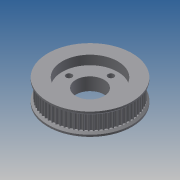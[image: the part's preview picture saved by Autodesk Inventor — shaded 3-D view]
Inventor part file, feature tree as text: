
AUTODESK INVENTOR PART (.ipt)
format: ipt  version: 2013 (Build 170138000, 138)  size: 355,840 bytes
history: native  units: mm
features: extrude x7, sketch x7, pattern_circular x2, chamfer x1, mirror x1
ambient origin geometry x8: Origin, YZ Plane, XZ Plane, XY Plane, X Axis, Y Axis, Z Axis, Center Point
bodies: Solid1 (feature_tree)
feature tree (18):
  extrude  "Extrusion1"  Depth=8.0mm TaperAngle=0.0deg
  extrude  "Extrusion3"  TaperAngle=0.0deg  [1 undecoded]
  extrude  "Extrusion4"  Depth=8.0mm TaperAngle=0.0deg
  pattern_circular  "Circular Pattern1"  Count=70 Angle=360.0deg
  extrude  "Extrusion5"  Depth=2.0mm TaperAngle=0.0deg
  chamfer  "Chamfer1"  Distance=1.0mm Angle=45.0deg
  mirror  "Mirror1"
  extrude  "Extrusion6"  Depth=2.0mm TaperAngle=0.0deg
  extrude  "Extrusion8"  Depth=5.0mm TaperAngle=0.0deg
  extrude  "Extrusion9"  Depth=11.5mm
  pattern_circular  "Circular Pattern2"  [2 undecoded]
  sketch  "Sketch1"  dims[d0=44.563384mm d9=8.0mm d10=0.0mm]
  sketch  "Sketch3"  dims[d22=0.254mm d23=0.0mm d24=0.0mm]
  sketch  "Sketch4"  dims[d25=1.59mm d27=8.0mm d28=0.0mm d29=700.0mm d30=360.0deg]
  sketch  "Sketch5"  dims[d33=1.0mm d34=2.0mm d35=0.0mm d36=1.0mm d37=2.0mm d38=45.0deg]
  sketch  "Sketch6"  dims[d39=15.5mm d41=2.0mm d42=0.0mm]
  sketch  "Sketch8"  dims[d46=30.5mm d48=5.0mm d49=0.0mm]
  sketch  "Sketch9"  dims[d50=3.3mm d52=11.5mm d53=5.0mm d54=0.0mm d55=40.0mm d56=360.0deg]
note: 3 required parameter values undecoded (feature->parameter linkage not recoverable at this tier; creation-order binding heuristic only, values carry confidence <= 0.55)
